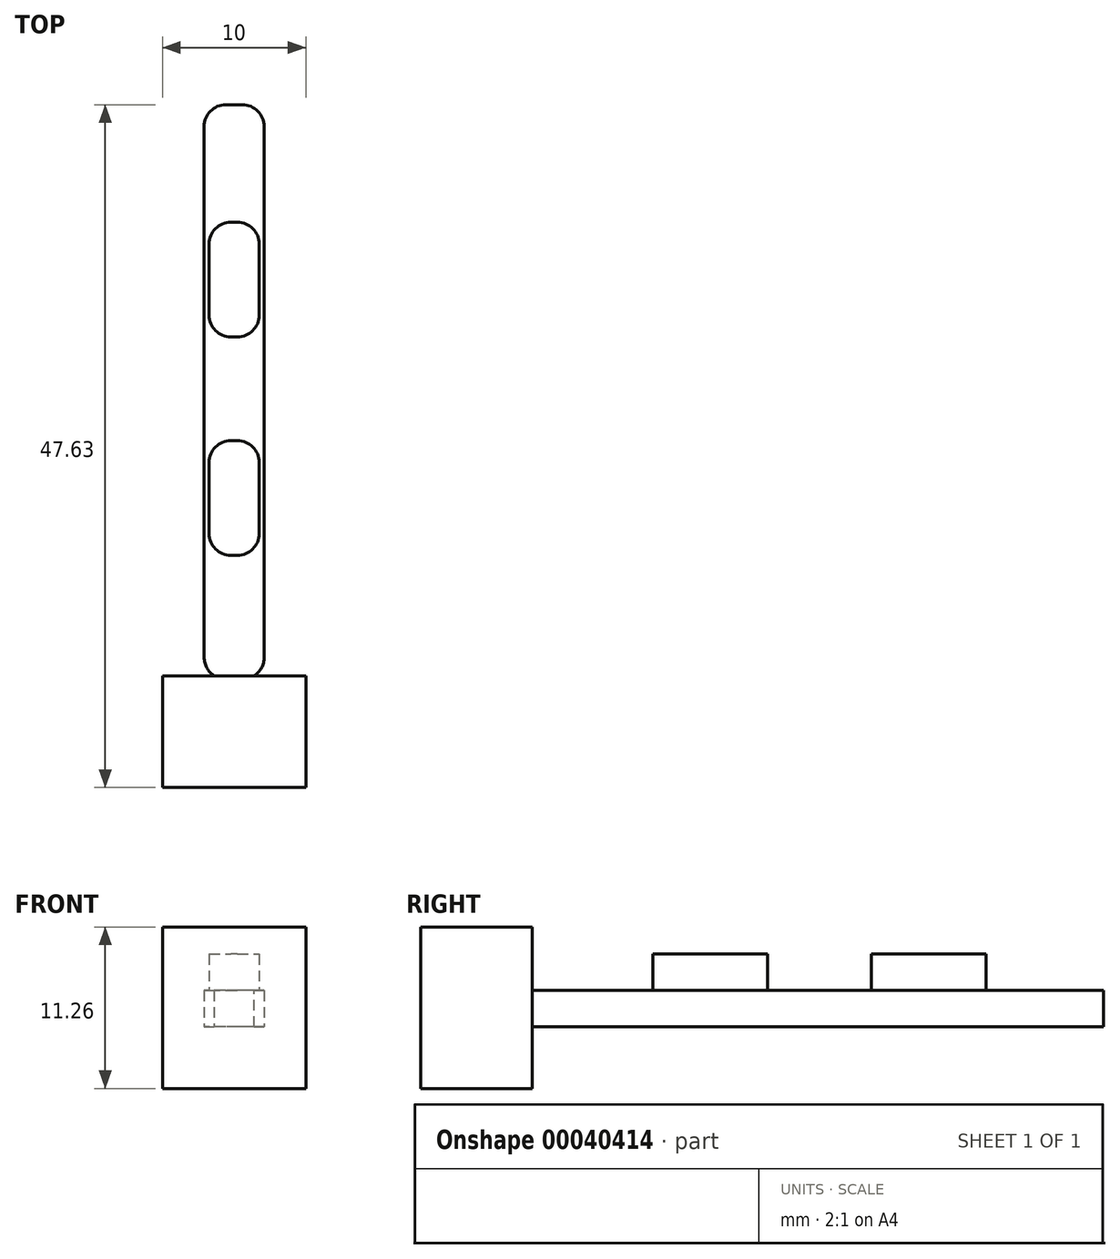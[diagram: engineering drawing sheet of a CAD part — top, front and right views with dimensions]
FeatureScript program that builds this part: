
annotation { "Feature Type Name" : "Feature", "Feature Type Description" : "" }
export const myFeature = defineFeature(function(context is Context, id is Id, definition is map)
    precondition{}
    {
        {
            var Q0;
            Q0=qCreatedBy(makeId("Top.planeOp"),FACE);
            var sketch = newSketch(context, id + "F0", { "sketchPlane" : qUnion([Q0])});
            skLineSegment(sketch, "E0.rect.bottom", {"start": v(2.1, -20.04) * mm, "end": v(-2.1, -20.04) * mm});
            skLineSegment(sketch, "E0.rect.top", {"start": v(2.1, 20.04) * mm, "end": v(-2.1, 20.04) * mm});
            skLineSegment(sketch, "E0.rect.left", {"start": v(2.1, -20.04) * mm, "end": v(2.1, 20.04) * mm});
            skLineSegment(sketch, "E0.rect.right", {"start": v(-2.1, -20.04) * mm, "end": v(-2.1, 20.04) * mm});
            skPoint(sketch, "E0.rect.middle", {"position": v(0, 0) * mm});
            skSolve(sketch);
        }
        {
            var Q0;
            Q0=qCreatedBy(makeId("Top.planeOp"),FACE);
            var sketch = newSketch(context, id + "F1", { "sketchPlane" : qUnion([Q0])});
            skLineSegment(sketch, "E1.rect.bottom", {"start": v(1.75, 3.84) * mm, "end": v(-1.75, 3.84) * mm});
            skLineSegment(sketch, "E1.rect.top", {"start": v(1.75, 11.84) * mm, "end": v(-1.75, 11.84) * mm});
            skLineSegment(sketch, "E1.rect.left", {"start": v(1.75, 3.84) * mm, "end": v(1.75, 11.84) * mm});
            skLineSegment(sketch, "E1.rect.right", {"start": v(-1.75, 3.84) * mm, "end": v(-1.75, 11.84) * mm});
            skPoint(sketch, "E1.rect.middle", {"position": v(0, 7.84) * mm});
            skLineSegment(sketch, "E2.rect.bottom", {"start": v(1.75, -11.4) * mm, "end": v(-1.75, -11.4) * mm});
            skLineSegment(sketch, "E2.rect.top", {"start": v(1.75, -3.4) * mm, "end": v(-1.75, -3.4) * mm});
            skLineSegment(sketch, "E2.rect.left", {"start": v(1.75, -11.4) * mm, "end": v(1.75, -3.4) * mm});
            skLineSegment(sketch, "E2.rect.right", {"start": v(-1.75, -11.4) * mm, "end": v(-1.75, -3.4) * mm});
            skPoint(sketch, "E2.rect.middle", {"position": v(0, -7.4) * mm});
            skSolve(sketch);
        }
        {
            var Q0;
            Q0=makeQuery(id+"F0.imprint","IMPRINT",FACE,{"disambiguationData":[TD([[makeQuery(id+"F0.imprint","IMPRINT",EDGE,{"derivedFrom":sQuery(id+"F0.wireOp",EDGE,"E0.rect.bottom")}),-1.0]])]});
            extrude(context, id + "F2", {"entities" : qUnion([Q0]), "depth" : 2.54 * mm});
        }
        {
            var Q0;
            Q0 = qSketchRegion(id + "F1", true);
            extrude(context, id + "F3", {"entities" : qUnion([Q0]), "operationType" : NewBodyOperationType.ADD, "depth" : 5.08 * mm});
        }
        {
            var Q0;
            Q0=makeQuery(id+"F3.opExtrude","SWEPT_EDGE",EDGE,{"disambiguationData":[OSD([sQuery(id+"F1.wireOp",EDGE,"E1.rect.top"),sQuery(id+"F1.wireOp",EDGE,"E1.rect.right")])]});
            fillet(context, id + "F4", {"entities" : qUnion([Q0]), "radius" : 1.52 * mm, "tangentPropagation" : true, "allowEdgeOverflow" : false});
        }
        {
            var Q0;
            Q0=makeQuery(id+"F3.opExtrude","SWEPT_EDGE",EDGE,{"disambiguationData":[OSD([sQuery(id+"F1.wireOp",EDGE,"E1.rect.top"),sQuery(id+"F1.wireOp",EDGE,"E1.rect.left")])]});
            var Q1;
            Q1=makeQuery(id+"F3.opExtrude","SWEPT_EDGE",EDGE,{"disambiguationData":[OSD([sQuery(id+"F1.wireOp",EDGE,"E1.rect.bottom"),sQuery(id+"F1.wireOp",EDGE,"E1.rect.left")])]});
            var Q2;
            Q2=makeQuery(id+"F3.opExtrude","SWEPT_EDGE",EDGE,{"disambiguationData":[OSD([sQuery(id+"F1.wireOp",EDGE,"E2.rect.top"),sQuery(id+"F1.wireOp",EDGE,"E2.rect.left")])]});
            var Q3;
            Q3=makeQuery(id+"F3.opExtrude","SWEPT_EDGE",EDGE,{"disambiguationData":[OSD([sQuery(id+"F1.wireOp",EDGE,"E2.rect.bottom"),sQuery(id+"F1.wireOp",EDGE,"E2.rect.left")])]});
            var Q4;
            Q4=makeQuery(id+"F3.opExtrude","SWEPT_EDGE",EDGE,{"disambiguationData":[OSD([sQuery(id+"F1.wireOp",EDGE,"E1.rect.bottom"),sQuery(id+"F1.wireOp",EDGE,"E1.rect.right")])]});
            var Q5;
            Q5=makeQuery(id+"F3.opExtrude","SWEPT_EDGE",EDGE,{"disambiguationData":[OSD([sQuery(id+"F1.wireOp",EDGE,"E2.rect.bottom"),sQuery(id+"F1.wireOp",EDGE,"E2.rect.right")])]});
            var Q6;
            Q6=makeQuery(id+"F3.opExtrude","SWEPT_EDGE",EDGE,{"disambiguationData":[OSD([sQuery(id+"F1.wireOp",EDGE,"E2.rect.top"),sQuery(id+"F1.wireOp",EDGE,"E2.rect.right")])]});
            fillet(context, id + "F5", {"entities" : qUnion([Q0, Q1, Q2, Q3, Q4, Q5, Q6]), "radius" : 1.52 * mm, "tangentPropagation" : true, "allowEdgeOverflow" : false});
        }
        {
            var Q0;
            Q0=makeQuery(id+"F2.opExtrude","SWEPT_EDGE",EDGE,{"disambiguationData":[OSD([sQuery(id+"F0.wireOp",EDGE,"E0.rect.top"),sQuery(id+"F0.wireOp",EDGE,"E0.rect.right")])]});
            var Q1;
            Q1=makeQuery(id+"F2.opExtrude","SWEPT_EDGE",EDGE,{"disambiguationData":[OSD([sQuery(id+"F0.wireOp",EDGE,"E0.rect.top"),sQuery(id+"F0.wireOp",EDGE,"E0.rect.left")])]});
            var Q2;
            Q2=makeQuery(id+"F2.opExtrude","SWEPT_EDGE",EDGE,{"disambiguationData":[OSD([sQuery(id+"F0.wireOp",EDGE,"E0.rect.bottom"),sQuery(id+"F0.wireOp",EDGE,"E0.rect.left")])]});
            var Q3;
            Q3=makeQuery(id+"F2.opExtrude","SWEPT_EDGE",EDGE,{"disambiguationData":[OSD([sQuery(id+"F0.wireOp",EDGE,"E0.rect.bottom"),sQuery(id+"F0.wireOp",EDGE,"E0.rect.right")])]});
            fillet(context, id + "F6", {"entities" : qUnion([Q0, Q1, Q2, Q3]), "radius" : 1.52 * mm, "tangentPropagation" : true, "allowEdgeOverflow" : false});
        }
        {
            var Q0;
            Q0=qCreatedBy(makeId("Right.planeOp"),FACE);
            var sketch = newSketch(context, id + "F7", { "sketchPlane" : qUnion([Q0])});
            skLineSegment(sketch, "E3.rect.bottom", {"start": v(-19.8, -4.29) * mm, "end": v(-27.6, -4.29) * mm});
            skLineSegment(sketch, "E3.rect.top", {"start": v(-19.8, 6.97) * mm, "end": v(-27.6, 6.97) * mm});
            skLineSegment(sketch, "E3.rect.left", {"start": v(-19.8, -4.29) * mm, "end": v(-19.8, 6.97) * mm});
            skLineSegment(sketch, "E3.rect.right", {"start": v(-27.6, -4.29) * mm, "end": v(-27.6, 6.97) * mm});
            skPoint(sketch, "E3.rect.middle", {"position": v(-23.7, 1.34) * mm});
            skSolve(sketch);
        }
        {
            var Q0;
            Q0 = qSketchRegion(id + "F7", true);
            extrude(context, id + "F8", {"entities" : qUnion([Q0]), "operationType" : NewBodyOperationType.ADD, "oppositeDirection" : true, "depth" : 5 * mm, "hasSecondDirection" : true, "secondDirectionOppositeDirection" : false, "secondDirectionDepth" : 5 * mm});
        }
    });
